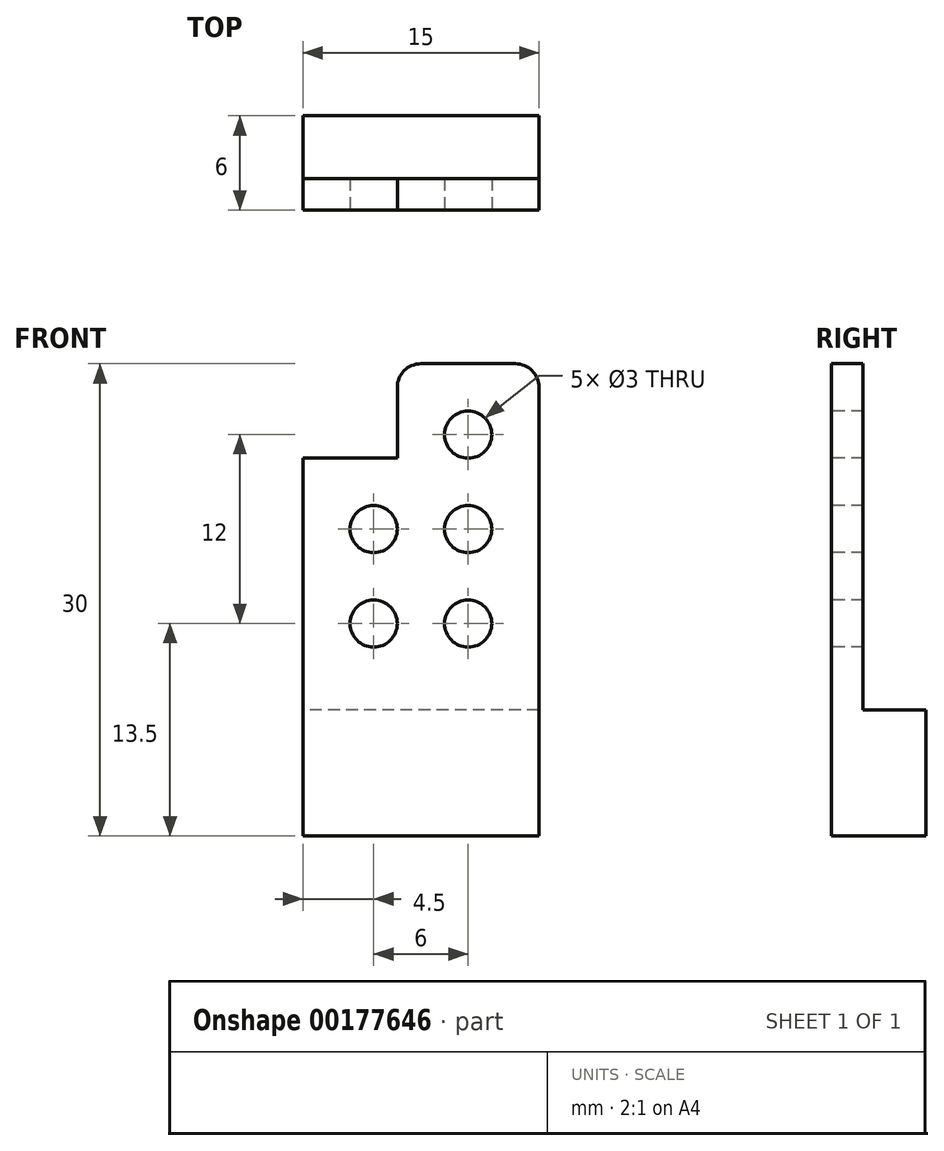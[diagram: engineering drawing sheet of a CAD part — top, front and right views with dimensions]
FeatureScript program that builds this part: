
annotation { "Feature Type Name" : "Feature", "Feature Type Description" : "" }
export const myFeature = defineFeature(function(context is Context, id is Id, definition is map)
    precondition{}
    {
        {
            var Q0;
            Q0=qCreatedBy(makeId("Front.planeOp"),FACE);
            var sketch = newSketch(context, id + "F0", { "sketchPlane" : qUnion([Q0])});
            skLineSegment(sketch, "E0.bottom", {"start": v(7.5, 7.5) * mm, "end": v(-7.5, 7.5) * mm});
            skLineSegment(sketch, "E0.top", {"start": v(7.5, -7.5) * mm, "end": v(-7.5, -7.5) * mm});
            skLineSegment(sketch, "E0.left", {"start": v(7.5, 7.5) * mm, "end": v(7.5, -7.5) * mm});
            skLineSegment(sketch, "E0.right", {"start": v(-7.5, 7.5) * mm, "end": v(-7.5, -7.5) * mm});
            skPoint(sketch, "E0.middle", {"position": v(0, 0) * mm});
            skSolve(sketch);
        }
        {
            var Q0;
            Q0 = qSketchRegion(id + "F0", true);
            extrude(context, id + "F1", {"entities" : qUnion([Q0]), "depth" : 2 * mm});
        }
        {
            var Q0;
            Q0=makeQuery(id+"F1.opExtrude","CAP_FACE",FACE,{"disambiguationData":[OSD([sQuery(id+"F0.wireOp",EDGE,"E0.bottom"),sQuery(id+"F0.wireOp",EDGE,"E0.top"),sQuery(id+"F0.wireOp",EDGE,"E0.left"),sQuery(id+"F0.wireOp",EDGE,"E0.right")])],"isStart":false});
            var sketch = newSketch(context, id + "F2", { "sketchPlane" : qUnion([Q0])});
            skCircle(sketch, "E1", {"center": v(3, 3) * mm, "radius": 1.5 * mm});
            skCircle(sketch, "E2", {"center": v(-3, 3) * mm, "radius": 1.5 * mm});
            skCircle(sketch, "E3", {"center": v(-3, -3) * mm, "radius": 1.5 * mm});
            skCircle(sketch, "E4", {"center": v(3, -3) * mm, "radius": 1.5 * mm});
            skSolve(sketch);
        }
        {
            var Q0;
            Q0 = qSketchRegion(id + "F2", true);
            extrude(context, id + "F3", {"entities" : qUnion([Q0]), "operationType" : NewBodyOperationType.REMOVE, "oppositeDirection" : true, "depth" : 25 * mm});
        }
        {
            var Q0;
            Q0=makeQuery(id+"F1.opExtrude","SWEPT_FACE",FACE,{"disambiguationData":[OSD([sQuery(id+"F0.wireOp",EDGE,"E0.bottom")])]});
            var sketch = newSketch(context, id + "F4", { "sketchPlane" : qUnion([Q0])});
            skLineSegment(sketch, "E5.bottom", {"start": v(7.5, 0) * mm, "end": v(-1.5, 0) * mm});
            skLineSegment(sketch, "E5.top", {"start": v(7.5, -2) * mm, "end": v(-1.5, -2) * mm});
            skLineSegment(sketch, "E5.left", {"start": v(7.5, 0) * mm, "end": v(7.5, -2) * mm});
            skLineSegment(sketch, "E5.right", {"start": v(-1.5, 0) * mm, "end": v(-1.5, -2) * mm});
            skSolve(sketch);
        }
        {
            var Q0;
            Q0 = qSketchRegion(id + "F4", true);
            extrude(context, id + "F5", {"entities" : qUnion([Q0]), "operationType" : NewBodyOperationType.ADD, "depth" : 6 * mm});
        }
        {
            var Q0;
            Q0=makeQuery(id+"F5.boolean.opBoolean","MERGE",FACE,{"derivedFrom":[makeQuery(id+"F1.opExtrude","CAP_FACE",FACE,{"disambiguationData":[OSD([sQuery(id+"F0.wireOp",EDGE,"E0.bottom"),sQuery(id+"F0.wireOp",EDGE,"E0.top"),sQuery(id+"F0.wireOp",EDGE,"E0.left"),sQuery(id+"F0.wireOp",EDGE,"E0.right")])],"isStart":false}),makeQuery(id+"F5.opExtrude","SWEPT_FACE",FACE,{"disambiguationData":[OSD([sQuery(id+"F4.wireOp",EDGE,"E5.top")])]})]});
            var sketch = newSketch(context, id + "F6", { "sketchPlane" : qUnion([Q0])});
            skCircle(sketch, "E6", {"center": v(3, 9) * mm, "radius": 1.5 * mm});
            skSolve(sketch);
        }
        {
            var Q0;
            Q0 = qSketchRegion(id + "F6", true);
            extrude(context, id + "F7", {"entities" : qUnion([Q0]), "operationType" : NewBodyOperationType.REMOVE, "oppositeDirection" : true, "depth" : 25 * mm});
        }
        {
            var Q0;
            Q0=makeQuery(id+"F5.opExtrude","CAP_EDGE",EDGE,{"disambiguationData":[OSD([sQuery(id+"F4.wireOp",EDGE,"E5.left")])],"isStart":false});
            var Q1;
            Q1=makeQuery(id+"F5.opExtrude","CAP_EDGE",EDGE,{"disambiguationData":[OSD([sQuery(id+"F4.wireOp",EDGE,"E5.right")])],"isStart":false});
            var Q2;
            Q2=makeQuery(id+"F5.opExtrude","CAP_EDGE",EDGE,{"disambiguationData":[OSD([sQuery(id+"F4.wireOp",EDGE,"E5.right")])],"isStart":true});
            fillet(context, id + "F8", {"entities" : qUnion([Q0, Q1, Q2]), "radius" : 1.5 * mm, "tangentPropagation" : true, "allowEdgeOverflow" : false});
        }
        {
            var Q0;
            Q0=makeQuery(id+"F1.opExtrude","SWEPT_FACE",FACE,{"disambiguationData":[OSD([sQuery(id+"F0.wireOp",EDGE,"E0.top")])]});
            var sketch = newSketch(context, id + "F9", { "sketchPlane" : qUnion([Q0])});
            skLineSegment(sketch, "E7.bottom", {"start": v(-7.5, 2) * mm, "end": v(7.5, 2) * mm});
            skLineSegment(sketch, "E7.top", {"start": v(-7.5, 0) * mm, "end": v(7.5, 0) * mm});
            skLineSegment(sketch, "E7.left", {"start": v(-7.5, 2) * mm, "end": v(-7.5, 0) * mm});
            skLineSegment(sketch, "E7.right", {"start": v(7.5, 2) * mm, "end": v(7.5, 0) * mm});
            skSolve(sketch);
        }
        {
            var Q0;
            Q0 = qSketchRegion(id + "F9", true);
            extrude(context, id + "F10", {"entities" : qUnion([Q0]), "operationType" : NewBodyOperationType.ADD, "depth" : 1 * mm});
        }
        {
            var Q0;
            Q0=makeQuery(id+"F10.opExtrude","CAP_FACE",FACE,{"disambiguationData":[OSD([sQuery(id+"F9.wireOp",EDGE,"E7.bottom"),sQuery(id+"F9.wireOp",EDGE,"E7.top"),sQuery(id+"F9.wireOp",EDGE,"E7.left"),sQuery(id+"F9.wireOp",EDGE,"E7.right")])],"isStart":false});
            var sketch = newSketch(context, id + "F11", { "sketchPlane" : qUnion([Q0])});
            skLineSegment(sketch, "E8.bottom", {"start": v(-7.5, 2) * mm, "end": v(7.5, 2) * mm});
            skLineSegment(sketch, "E8.top", {"start": v(-7.5, -4) * mm, "end": v(7.5, -4) * mm});
            skLineSegment(sketch, "E8.left", {"start": v(-7.5, 2) * mm, "end": v(-7.5, -4) * mm});
            skLineSegment(sketch, "E8.right", {"start": v(7.5, 2) * mm, "end": v(7.5, -4) * mm});
            skSolve(sketch);
        }
        {
            var Q0;
            Q0 = qSketchRegion(id + "F11", true);
            extrude(context, id + "F12", {"entities" : qUnion([Q0]), "operationType" : NewBodyOperationType.ADD, "depth" : 8 * mm});
        }
    });
